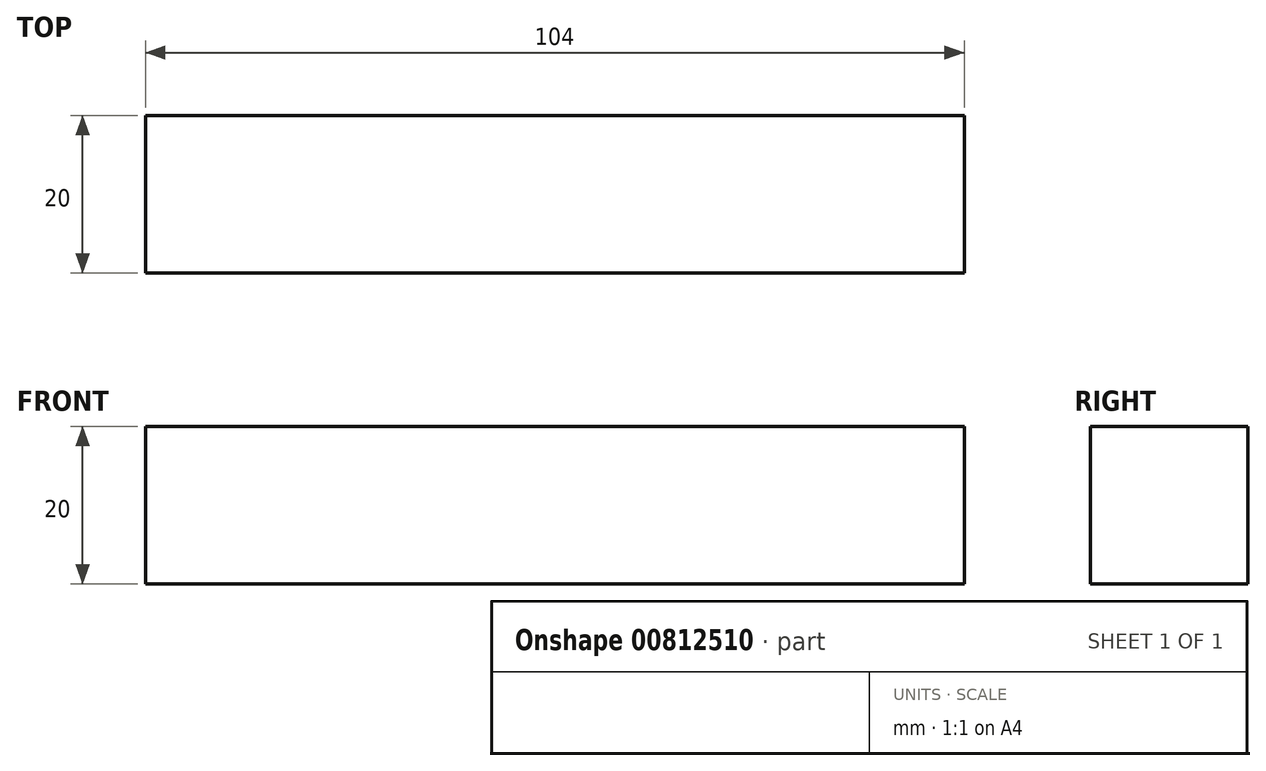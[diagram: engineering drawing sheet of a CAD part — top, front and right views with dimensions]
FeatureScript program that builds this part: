
annotation { "Feature Type Name" : "Feature", "Feature Type Description" : "" }
export const myFeature = defineFeature(function(context is Context, id is Id, definition is map)
    precondition{}
    {
        {
            var Q0;
            Q0=qCreatedBy(makeId("Right.planeOp"),FACE);
            var sketch = newSketch(context, id + "F0", { "sketchPlane" : qUnion([Q0])});
            skLineSegment(sketch, "E0.bottom", {"start": v(-10, 10) * mm, "end": v(10, 10) * mm});
            skLineSegment(sketch, "E0.top", {"start": v(-10, -10) * mm, "end": v(10, -10) * mm});
            skLineSegment(sketch, "E0.left", {"start": v(-10, 10) * mm, "end": v(-10, -10) * mm});
            skLineSegment(sketch, "E0.right", {"start": v(10, 10) * mm, "end": v(10, -10) * mm});
            skSolve(sketch);
        }
        {
            var Q0;
            Q0 = qSketchRegion(id + "F0", true);
            extrude(context, id + "F1", {"entities" : qUnion([Q0]), "depth" : 104 * mm, "offsetDistance" : 25 * mm});
        }
    });
